# Revit family: Tyco_FireDtctnAlmCtrlIndctEquip_Zettler-Profile2-8LoopAddressableCtrlIndctPanel
name_source: partatom
category: Fire Alarm Devices
revit_build: Autodesk Revit MEP 2013 (Build: 20120221_2030(x64)
units: mm (PartAtom-declared; Revit-internal decimal feet)

## types (2) — shared parameters
AssetType = Moveable
Brand = Zettler
Zettler
Category = Ee_40_15_75
Color = Grey
Default Elevation = 1200 mm
Depth = 221 mm  [stored 0.725066 ft]
DurationUnit = Year
ElectricalDeviceNominalPower = 0 VA
GUIPanelOffset = 464 mm  [stored 1.52231 ft]
GUIPanelWidth = 229 mm
HasProtectiveEarth = Yes
Height = 580 mm  [stored 1.90289 ft]
IfcExportAs = IfcDistributionElement
IfcExportType = NOTDEFINED
IfcTypeObject = IfcBuildingElementProxy
Manufacturer = Tyco Fire Protection Products
ManufacturerName = Tyco Fire Protection Products
ManufacturerURL = www.zettlerfire.com
Material = Mild steel
NBSDescription = Fire detection and alarm control and indicating equipment (CIE)
NBSReference = 90-75-30/380
NoOfLoops = 2 to 8
NoOfZonesSupported = 240
NominalCurrent = 2 A
NominalFrequencyRange = 50/60 Hz
NominalHeight = 580 mm  [stored 1.90289 ft]
NominalLength = 221 mm  [stored 0.725066 ft]
NominalVoltage = 230 V AC
NominalWidth = 458 mm
OperationTemperatureRange = -8 °C to +55 °C
PhaseAngle = 0.00°
ProductInformation = http://www.zettlerfire.com
RelativeHumidity = 90% RH continuous (non-condensing)
Shape = Rectangle
StorageTemperature = -20 °C to +70 °C
TotalNoOfAddresses = 500/2000
URL = http://www.zettlerfire.com
Uniclass2 = Ee_40_15_75
UsageCurrent = 0 A
Version = 1
WarrantyDurationLabor = 1.5 years
WarrantyDurationParts = 1.5 years
WarrantyDurationUnit = Year
Width = 458 mm

## per-type parameters (varying)
| type | BIMObjectName | ComponentWeight | Description | Model | ModelNumber | Name | NoOfZonalLEDs | NumberOfPoles | ProductCodes | ProductSpecification | ShowZoneLEDs |
| With80ZoneLEDsAnd2x38AhBatteries-P885D | Tyco_FireDtctnAlmCtrlIndctEquip_Zettler-Profile2-8LoopAddressableCtrlIndctPanel With80ZoneLEDsAnd2x38AhBatteries-P885D | 15.2 Kg | Zettler-Profile 2-8 Loop Addressable Control and Indicating Panel with 80 Zone LEDs and 2*38Ah Batteries | P885D | P885D | P885D Profile 2-8 Loop Addressable Control and Indicating Panel with 80 Zone LEDs and 2*38Ah Batteries | 80 | 1 | 557.200.555 | P885D Profile 2-8 Loop Addressable Control and Indicating Panel with 80 Zone LEDs and 2*38Ah Batteries | Yes |
| with2x38AhBatteries-P805D | Tyco_FireDtctnAlmCtrlIndctEquip_Zettler-Profile2-8LoopAddressableCtrlIndctPanel with2x38AhBatteries-P805D | 15.1 Kg | Zettler-Profile 2-8 Loop Addressable Control and Indicating Panel with 2*38Ah Batteries | P805D | P805D | P805D Profile 2-8 Loop Addressable Control and Indicating Panel with 2*38Ah Batteries | 0 | 0 | 557.200.556 | P805D Profile 2-8 Loop Addressable Control and Indicating Panel with 2*38Ah Batteries | No |

note: [stored X ft] marks values corroborated as IEEE doubles in the binary element streams (Revit-internal decimal feet)

## geometry (parser evidence)
native form markers: Sweep x2
no freeform markers — native parametric forms only
